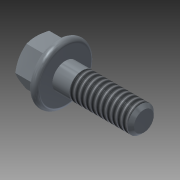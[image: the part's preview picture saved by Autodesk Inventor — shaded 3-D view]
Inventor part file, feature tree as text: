
AUTODESK INVENTOR PART (.ipt)
format: ipt  version: 2014 (Build 180170000, 170)  size: 190,976 bytes
history: native  units: mm (DEFAULTED — no unit token found)
features: sketch x3, extrude x1, chamfer x1, plane x1
ambient origin geometry x7: Origin, YZ Plane, XZ Plane, X Axis, Y Axis, Z Axis, Center Point
bodies: Solid1 (feature_tree), Body (feature_tree)
feature tree (6):
  extrude  "Head"  Depth=19.05mm
  chamfer  "Chamfer1"  Distance=6.35mm
  plane  "Work Plane1"
  sketch  "Sketch1"  dims[d0=1.016mm d1=19.05mm]
  sketch  "Sketch2"  dims[d2=14.9352mm]
  sketch  "Sketch3"  dims[d3=14.224mm d4=6.35mm d5=3.2004mm d12=90.0deg d6=7.112mm d7=0.0mm d8=30.0deg d21=90.0deg d10=14.9352mm d11=0.0mm d13=0.779082mm d14=0.779081mm d15=6.35mm d16=6.35mm d17=0.0001mm d18=1.905mm d19=4.363323mm d20=0.0mm d22=9.525mm d23=9.525mm d39=45.0deg d40=0.0mm d41=0.0mm]
